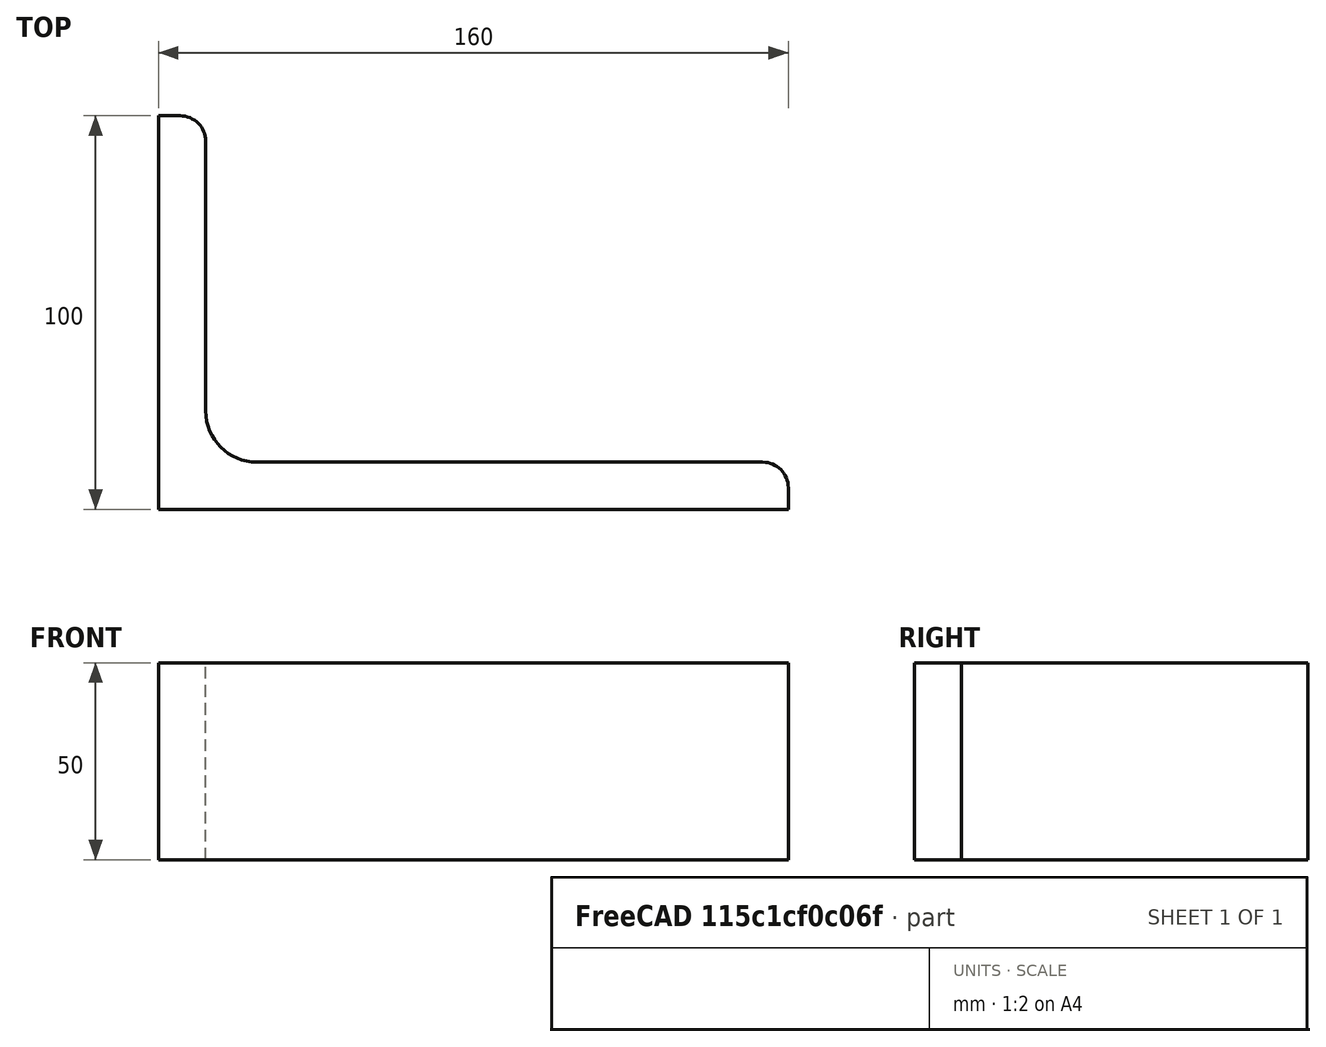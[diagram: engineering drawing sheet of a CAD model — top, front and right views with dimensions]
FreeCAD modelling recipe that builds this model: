
FCSTD DOCUMENT  (FreeCAD 0.15R4671 (Git))
Label: Angle Bar 160x100x12 EN10056 S235JR
License: All rights reserved
LicenseURL: http://en.wikipedia.org/wiki/All_rights_reserved
objects: Sketcher::SketchObject×1, Part::Extrusion×1
note: 2 computed .brp shape members not serialized (recipe doc carries the construction recipe); baked Part::Feature solids carry a one-line shape summary decoded from their .brp

FEATURE [Sketcher::SketchObject] Sketch
  sketch-geometry (9):
    g0: LineSegment StartX=0 StartY=0 StartZ=0 EndX=160 EndY=0 EndZ=0
    g1: LineSegment StartX=160 StartY=0 StartZ=0 EndX=160 EndY=5.5 EndZ=0
    g2: LineSegment StartX=153.5 StartY=12 StartZ=0 EndX=25 EndY=12 EndZ=0
    g3: LineSegment StartX=0 StartY=0 StartZ=0 EndX=0 EndY=100 EndZ=0
    g4: LineSegment StartX=0 StartY=100 StartZ=0 EndX=5.5 EndY=100 EndZ=0
    g5: LineSegment StartX=12 StartY=93.5 StartZ=0 EndX=12 EndY=25 EndZ=0
    g6: ArcOfCircle CenterX=25 CenterY=25 CenterZ=0 NormalX=0 NormalY=0 NormalZ=1 Radius=13 StartAngle=3.14159 EndAngle=4.71239
    g7: ArcOfCircle CenterX=5.5 CenterY=93.5 CenterZ=0 NormalX=0 NormalY=0 NormalZ=1 Radius=6.5 StartAngle=0 EndAngle=1.5708
    g8: ArcOfCircle CenterX=153.5 CenterY=5.5 CenterZ=0 NormalX=0 NormalY=0 NormalZ=1 Radius=6.5 StartAngle=0 EndAngle=1.5708
  constraints (23):
    c: Coincident(g0,g-1)
    c: Horizontal(g0)
    c: Coincident(g1,g0)
    c: Vertical(g1)
    c: Horizontal(g2)
    c: Coincident(g3,g-1)
    c: Vertical(g3)
    c: Coincident(g4,g3)
    c: Horizontal(g4)
    c: Vertical(g5)
    c: Tangent(g5,g6) = -1.5708
    c: Tangent(g2,g6) = 1.5708
    c: Tangent(g4,g7) = 1.5708
    c: Tangent(g5,g7) = 1.5708
    c: Tangent(g2,g8) = -1.5708
    c: Tangent(g1,g8) = -1.5708
    c: DistanceX(g0) = 160
    c: DistanceY(g3) = 100
    c: DistanceY(g0,g2) = 12
    c: DistanceX(g3,g5) = 12
    c: Radius(g6) = 13
    c: Radius(g8) = 6.5
    c: Radius(g7) = 6.5
FEATURE [Part::Extrusion] Extrude  label="Angle Bar 160x100x12 EN10056 S235JR"
  Base = -> Sketch
  Dir = (0,0,50)
  Solid = true
